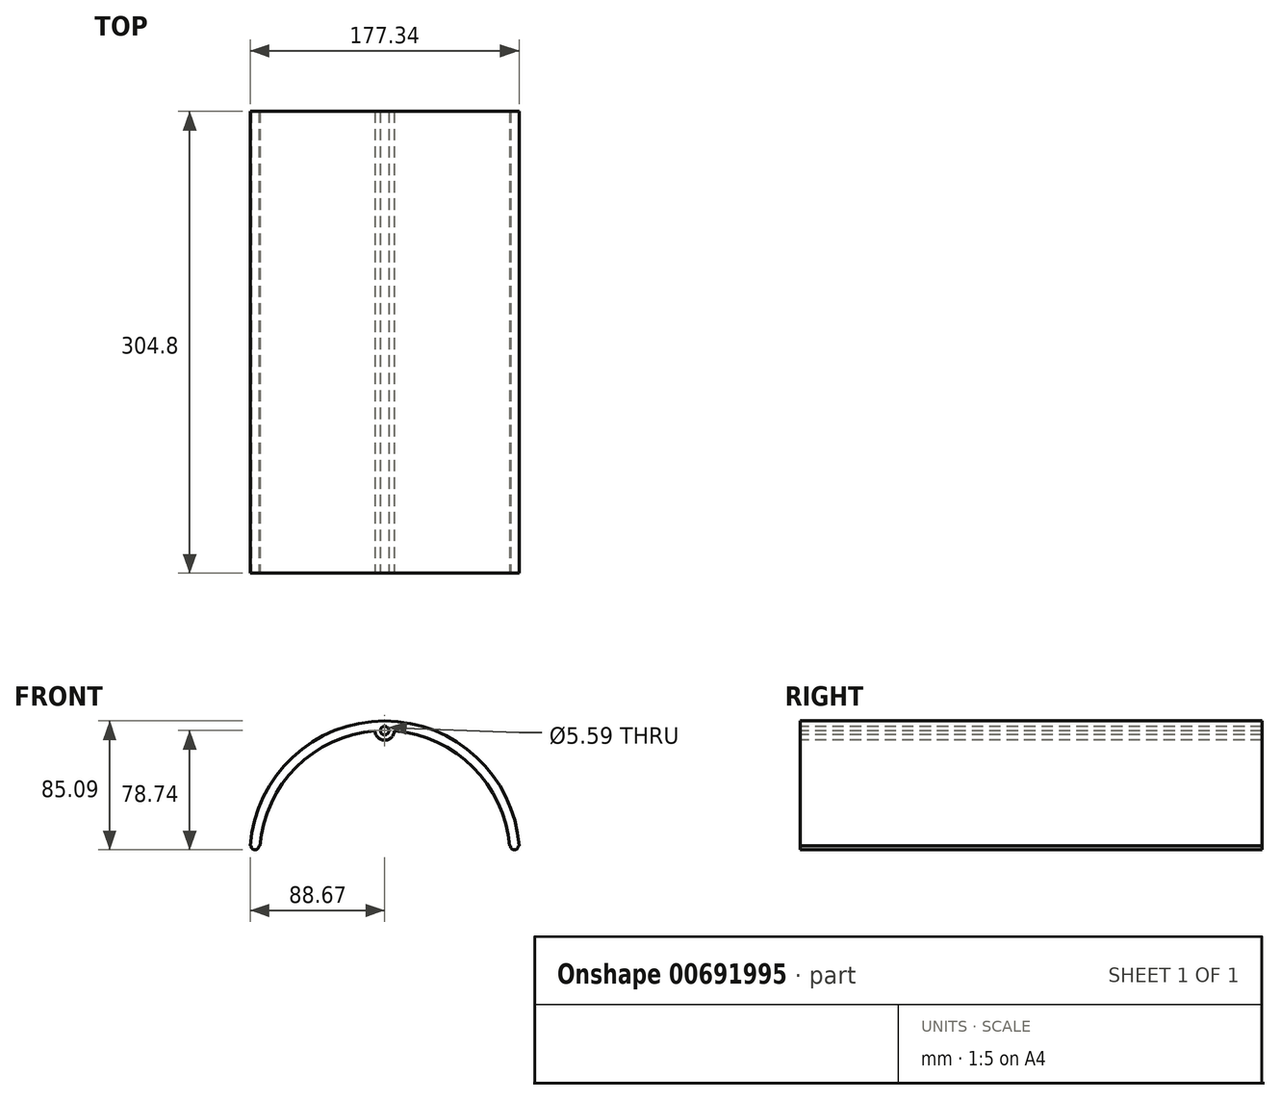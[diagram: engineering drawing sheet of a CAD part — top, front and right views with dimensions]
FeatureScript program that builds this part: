
annotation { "Feature Type Name" : "Feature", "Feature Type Description" : "" }
export const myFeature = defineFeature(function(context is Context, id is Id, definition is map)
    precondition{}
    {
        {
            var Q0;
            Q0=qCreatedBy(makeId("Front.planeOp"),FACE);
            var sketch = newSketch(context, id + "F0", { "sketchPlane" : qUnion([Q0])});
            skCircle(sketch, "E0", {"center": v(0, 0) * mm, "radius": 88.9 * mm});
            skSolve(sketch);
        }
        {
            var Q0;
            Q0=makeQuery(id+"F0.imprint","IMPRINT",FACE,{"disambiguationData":[TD([[makeQuery(id+"F0.imprint","IMPRINT",EDGE,{"derivedFrom":sQuery(id+"F0.wireOp",EDGE,"E0")}),1.0]])]});
            extrude(context, id + "F1", {"entities" : qUnion([Q0]), "oppositeDirection" : true, "depth" : 152.4 * mm, "offsetDistance" : 25.4 * mm});
        }
        {
            var Q0;
            Q0=makeQuery(id+"F1.opExtrude","CAP_FACE",FACE,{"disambiguationData":[OSD([sQuery(id+"F0.wireOp",EDGE,"E0")])],"isStart":true});
            var sketch = newSketch(context, id + "F2", { "sketchPlane" : qUnion([Q0])});
            skArc(sketch, "E1", {"start": v(2.8, -82.5) * mm, "mid": v(58.37, -58.37) * mm, "end": v(82.5, -2.8) * mm});
            skLineSegment(sketch, "E2", {"start": v(0, 0) * mm, "end": v(0, 79.76) * mm});
            skLineSegment(sketch, "E3", {"start": v(0, 0) * mm, "end": v(0, -79.76) * mm});
            skLineSegment(sketch, "E4", {"start": v(0, 0) * mm, "end": v(79.76, 0) * mm});
            skLineSegment(sketch, "E5", {"start": v(0, 0) * mm, "end": v(-79.76, 0) * mm});
            skCircle(sketch, "E6", {"center": v(0, 82.55) * mm, "radius": 2.8 * mm});
            skCircle(sketch, "E7", {"center": v(-82.55, 0) * mm, "radius": 2.8 * mm});
            skCircle(sketch, "E8", {"center": v(82.55, 0) * mm, "radius": 2.8 * mm});
            skCircle(sketch, "E9", {"center": v(0, -82.55) * mm, "radius": 2.8 * mm});
            skArc(sketch, "E10.trimOffspring", {"start": v(82.5, 2.8) * mm, "mid": v(58.37, 58.37) * mm, "end": v(2.8, 82.5) * mm});
            skArc(sketch, "E11.trimOffspring", {"start": v(-2.8, 82.5) * mm, "mid": v(-58.37, 58.37) * mm, "end": v(-82.5, 2.8) * mm});
            skArc(sketch, "E12.trimOffspring", {"start": v(-82.5, -2.8) * mm, "mid": v(-58.37, -58.37) * mm, "end": v(-2.8, -82.5) * mm});
            skSolve(sketch);
        }
        {
            var Q0;
            Q0=makeQuery(id+"F0.imprint","IMPRINT",FACE,{"disambiguationData":[TD([[makeQuery(id+"F0.imprint","IMPRINT",EDGE,{"derivedFrom":sQuery(id+"F0.wireOp",EDGE,"E0")}),1.0]])]});
            var sketch = newSketch(context, id + "F3", { "sketchPlane" : qUnion([Q0])});
            skCircle(sketch, "E13", {"center": v(0, 82.55) * mm, "radius": 6.35 * mm});
            skCircle(sketch, "E14", {"center": v(82.55, 0) * mm, "radius": 6.35 * mm});
            skCircle(sketch, "E15", {"center": v(-82.55, 0) * mm, "radius": 6.35 * mm});
            skCircle(sketch, "E16", {"center": v(0, -82.55) * mm, "radius": 6.35 * mm});
            skArc(sketch, "E17", {"start": v(-6.35, 82.3) * mm, "mid": v(-58.37, 58.37) * mm, "end": v(-82.3, 6.35) * mm});
            skArc(sketch, "E18.trimOffspring", {"start": v(82.3, 6.35) * mm, "mid": v(58.37, 58.37) * mm, "end": v(6.35, 82.3) * mm});
            skArc(sketch, "E19.trimOffspring", {"start": v(6.35, -82.3) * mm, "mid": v(58.37, -58.37) * mm, "end": v(82.3, -6.35) * mm});
            skArc(sketch, "E20.trimOffspring", {"start": v(-82.3, -6.35) * mm, "mid": v(-58.37, -58.37) * mm, "end": v(-6.35, -82.3) * mm});
            skSolve(sketch);
        }
        {
            var Q0;
            {var subQ0=sQuery(id+"F3.wireOp",EDGE,"E17");Q0=makeQuery(id+"F3.imprint","IMPRINT",FACE,{"disambiguationData":[TD([[makeQuery(id+"F3.imprint","IMPRINT",EDGE,{"derivedFrom":subQ0}),1.0]])]});}
            extrude(context, id + "F4", {"entities" : qUnion([Q0]), "operationType" : NewBodyOperationType.REMOVE, "endBound" : BoundingType.THROUGH_ALL, "oppositeDirection" : true, "depth" : 25.4 * mm, "offsetDistance" : 25.4 * mm});
        }
        {
            var Q0;
            {var subQ0=sQuery(id+"F2.wireOp",EDGE,"E6");var subQ1=makeQuery(id+"F2.imprint","INTERSECT",VERTEX,{"derivedFrom":[sQuery(id+"F2.wireOp",EDGE,"E2"),subQ0]});Q0=makeQuery(id+"F2.imprint","IMPRINT",FACE,{"disambiguationData":[TD([[makeQuery(id+"F2.imprint","IMPRINT",EDGE,{"disambiguationData":[TD([[subQ1,1.0]])],"derivedFrom":subQ0}),1.0]])]});}
            var Q1;
            {var subQ0=sQuery(id+"F2.wireOp",EDGE,"E7");var subQ1=makeQuery(id+"F2.imprint","INTERSECT",VERTEX,{"derivedFrom":[sQuery(id+"F2.wireOp",EDGE,"E5"),subQ0]});Q1=makeQuery(id+"F2.imprint","IMPRINT",FACE,{"disambiguationData":[TD([[makeQuery(id+"F2.imprint","IMPRINT",EDGE,{"disambiguationData":[TD([[subQ1,-1.0]])],"derivedFrom":subQ0}),1.0]])]});}
            var Q2;
            {var subQ0=sQuery(id+"F2.wireOp",EDGE,"E8");var subQ1=makeQuery(id+"F2.imprint","INTERSECT",VERTEX,{"derivedFrom":[sQuery(id+"F2.wireOp",EDGE,"E4"),subQ0]});Q2=makeQuery(id+"F2.imprint","IMPRINT",FACE,{"disambiguationData":[TD([[makeQuery(id+"F2.imprint","IMPRINT",EDGE,{"disambiguationData":[TD([[subQ1,1.0]])],"derivedFrom":subQ0}),1.0]])]});}
            var Q3;
            {var subQ0=sQuery(id+"F2.wireOp",EDGE,"E9");var subQ1=makeQuery(id+"F2.imprint","INTERSECT",VERTEX,{"derivedFrom":[sQuery(id+"F2.wireOp",EDGE,"E1"),subQ0]});Q3=makeQuery(id+"F2.imprint","IMPRINT",FACE,{"disambiguationData":[TD([[makeQuery(id+"F2.imprint","IMPRINT",EDGE,{"disambiguationData":[TD([[subQ1,-1.0]])],"derivedFrom":subQ0}),1.0]])]});}
            extrude(context, id + "F5", {"entities" : qUnion([Q0, Q1, Q2, Q3]), "operationType" : NewBodyOperationType.REMOVE, "endBound" : BoundingType.THROUGH_ALL, "oppositeDirection" : true, "depth" : 25.4 * mm, "offsetDistance" : 25.4 * mm});
        }
        {
            var Q0;
            {var subQ0=sQuery(id+"F3.wireOp",EDGE,"E17");Q0=makeQuery(id+"F3.imprint","IMPRINT",FACE,{"disambiguationData":[TD([[makeQuery(id+"F3.imprint","IMPRINT",EDGE,{"derivedFrom":subQ0}),1.0]])]});}
            var sketch = newSketch(context, id + "F6", { "sketchPlane" : qUnion([Q0])});
            skLineSegment(sketch, "E21", {"start": v(0, 0) * mm, "end": v(82.55, 0) * mm});
            skLineSegment(sketch, "E22", {"start": v(88.9, 0) * mm, "end": v(88.9, 6.35) * mm});
            skPoint(sketch, "E23.end.orphan", {"position": v(88.9, -97.1) * mm});
            skLineSegment(sketch, "E24", {"start": v(0, 0) * mm, "end": v(-88.9, 0) * mm});
            skLineSegment(sketch, "E25", {"start": v(-88.9, 0) * mm, "end": v(-88.9, 6.35) * mm});
            skLineSegment(sketch, "E26", {"start": v(-88.9, 6.35) * mm, "end": v(-88.14, 6.35) * mm});
            skLineSegment(sketch, "E27", {"start": v(-82.55, 6.35) * mm, "end": v(-83.06, 6.35) * mm});
            skCircle(sketch, "E28", {"center": v(-85.6, 6.35) * mm, "radius": 2.54 * mm});
            skLineSegment(sketch, "E29", {"start": v(88.9, 0) * mm, "end": v(82.55, 0) * mm});
            skLineSegment(sketch, "E30", {"start": v(82.55, 6.35) * mm, "end": v(83.06, 6.35) * mm});
            skCircle(sketch, "E31", {"center": v(85.6, 6.35) * mm, "radius": 2.54 * mm});
            skLineSegment(sketch, "E32", {"start": v(88.9, 0) * mm, "end": v(118.6, -139.2) * mm});
            skLineSegment(sketch, "E33", {"start": v(118.6, -139.2) * mm, "end": v(-105.38, -144.1) * mm});
            skLineSegment(sketch, "E34", {"start": v(-105.38, -144.1) * mm, "end": v(-88.9, 0) * mm});
            skLineSegment(sketch, "E35.trimOffspring", {"start": v(88.14, 6.35) * mm, "end": v(88.9, 6.35) * mm});
            skLineSegment(sketch, "E36.trimOffspring", {"start": v(-82.55, 6.35) * mm, "end": v(83.06, 6.35) * mm});
            skLineSegment(sketch, "E37", {"start": v(88.9, 6.35) * mm, "end": v(-109.31, 6.35) * mm});
            skLineSegment(sketch, "E38", {"start": v(-109.31, 6.35) * mm, "end": v(-104.9, -139.88) * mm});
            skLineSegment(sketch, "E39", {"start": v(-104.9, -139.88) * mm, "end": v(179.33, -117.08) * mm});
            skLineSegment(sketch, "E40", {"start": v(179.33, -117.08) * mm, "end": v(106.4, 6.35) * mm});
            skLineSegment(sketch, "E41", {"start": v(106.4, 6.35) * mm, "end": v(88.9, 6.35) * mm});
            skSolve(sketch);
        }
        {
            var Q0;
            {var subQ4=sQuery(id+"F6.wireOp",EDGE,"E29");Q0=makeQuery(id+"F6.imprint","IMPRINT",FACE,{"disambiguationData":[TD([[makeQuery(id+"F6.imprint","IMPRINT",EDGE,{"derivedFrom":subQ4}),1.0]])]});}
            var Q1;
            {var subQ4=sQuery(id+"F6.wireOp",EDGE,"E22");Q1=makeQuery(id+"F6.imprint","IMPRINT",FACE,{"disambiguationData":[TD([[makeQuery(id+"F6.imprint","IMPRINT",EDGE,{"derivedFrom":subQ4}),-1.0]])]});}
            var Q2;
            {var subQ5=sQuery(id+"F6.wireOp",EDGE,"E22");Q2=makeQuery(id+"F6.imprint","IMPRINT",FACE,{"disambiguationData":[TD([[makeQuery(id+"F6.imprint","IMPRINT",EDGE,{"derivedFrom":subQ5}),1.0]])]});}
            var Q3;
            {var subQ7=sQuery(id+"F6.wireOp",EDGE,"E25");Q3=makeQuery(id+"F6.imprint","IMPRINT",FACE,{"disambiguationData":[TD([[makeQuery(id+"F6.imprint","IMPRINT",EDGE,{"derivedFrom":subQ7}),-1.0]])]});}
            extrude(context, id + "F7", {"entities" : qUnion([Q0, Q1, Q2, Q3]), "operationType" : NewBodyOperationType.REMOVE, "endBound" : BoundingType.THROUGH_ALL, "oppositeDirection" : true, "depth" : 25.4 * mm, "offsetDistance" : 25.4 * mm});
        }
        {
            var Q0;
            Q0=makeQuery(id+"F1.opExtrude","SWEPT_BODY",BODY,{"disambiguationData":[OSD([sQuery(id+"F0.wireOp",EDGE,"E0")])]});
            var Q1;
            {var subQ1=sQuery(id+"F2.wireOp",EDGE,"E1");Q1=makeQuery(id+"F2.imprint","IMPRINT",FACE,{"disambiguationData":[TD([[makeQuery(id+"F2.imprint","IMPRINT",EDGE,{"derivedFrom":subQ1}),-1.0]])]});}
            mirror(context, id + "F8", {"operationType" : NewBodyOperationType.ADD, "entities" : qUnion([Q0]), "mirrorPlane" : qUnion([Q1])});
        }
    });
